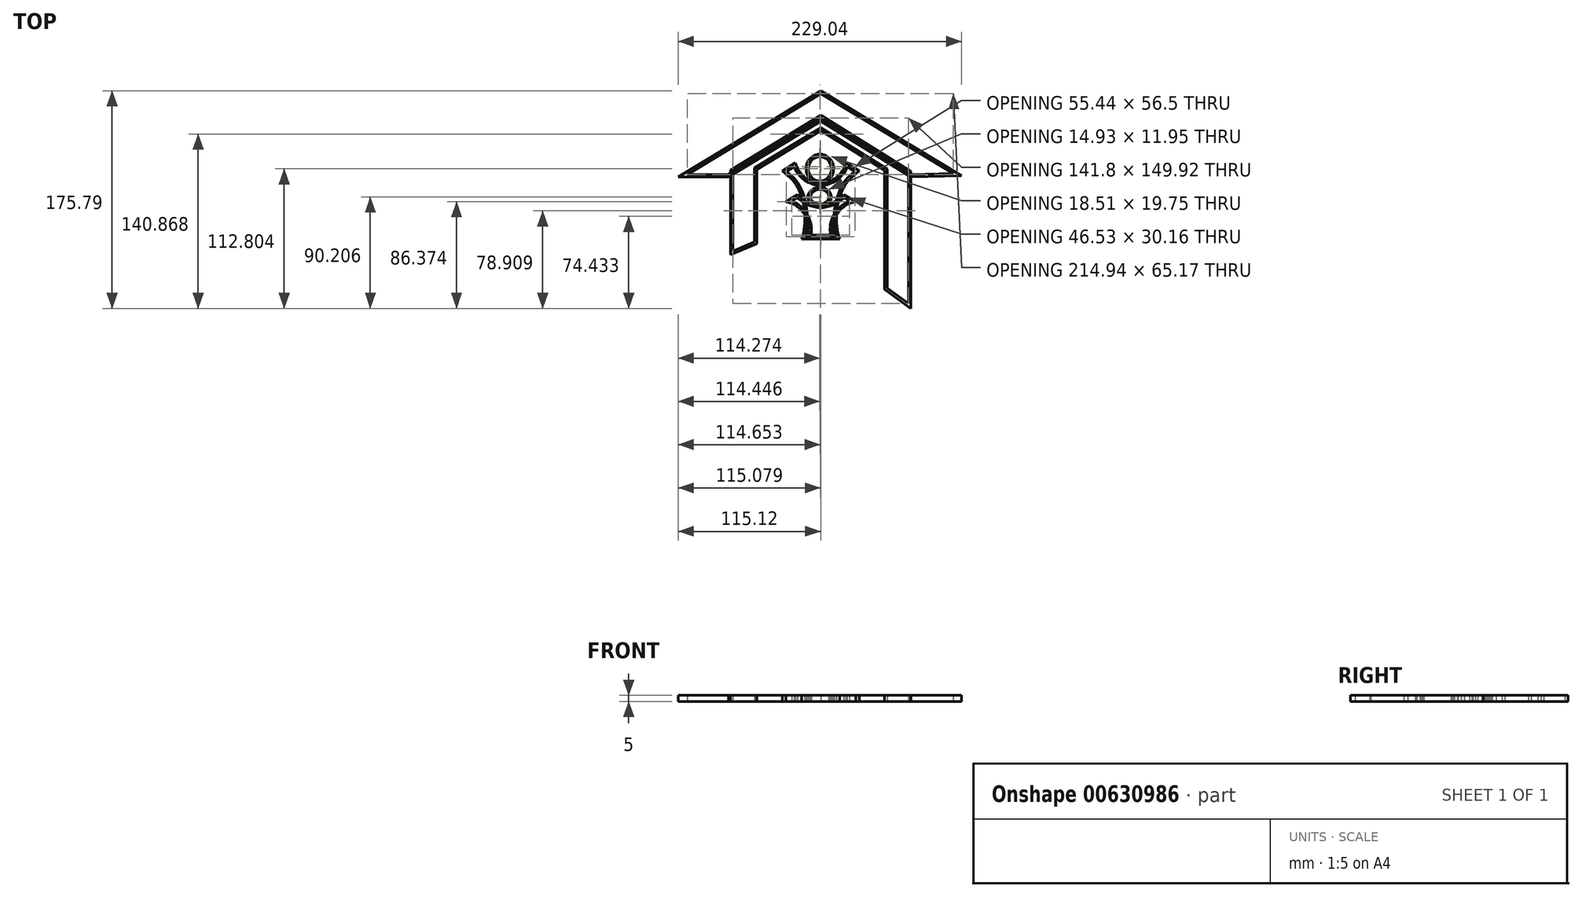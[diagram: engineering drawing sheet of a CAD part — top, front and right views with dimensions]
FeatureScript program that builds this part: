
annotation { "Feature Type Name" : "Feature", "Feature Type Description" : "" }
export const myFeature = defineFeature(function(context is Context, id is Id, definition is map)
    precondition{}
    {
        {
            var Q0;
            Q0=qCreatedBy(makeId("Top.planeOp"),FACE);
            var sketch = newSketch(context, id + "F0", { "sketchPlane" : qUnion([Q0])});
            skLineSegment(sketch, "E0", {"start": v(0, 74.4) * mm, "end": v(107, 10.1) * mm});
            skLineSegment(sketch, "E1", {"start": v(107, 10.1) * mm, "end": v(73.24, 9.22) * mm});
            skLineSegment(sketch, "E2", {"start": v(73.24, 9.22) * mm, "end": v(0, 54.8) * mm});
            skLineSegment(sketch, "E3", {"start": v(0, 54.8) * mm, "end": v(-74.92, 9.22) * mm});
            skLineSegment(sketch, "E4", {"start": v(-74.92, 9.22) * mm, "end": v(-107.94, 9.22) * mm});
            skLineSegment(sketch, "E5", {"start": v(-107.94, 9.22) * mm, "end": v(0, 74.4) * mm});
            skLineSegment(sketch, "E6", {"start": v(-70.94, 11.64) * mm, "end": v(-70.94, -52.76) * mm});
            skLineSegment(sketch, "E7", {"start": v(-70.94, -52.76) * mm, "end": v(-53.55, -45.28) * mm});
            skLineSegment(sketch, "E8", {"start": v(-53.55, -45.28) * mm, "end": v(-53.55, 14.44) * mm});
            skLineSegment(sketch, "E9", {"start": v(-53.55, 14.44) * mm, "end": v(0, 47.03) * mm});
            skLineSegment(sketch, "E10", {"start": v(0, 47.03) * mm, "end": v(53.66, 13.63) * mm});
            skLineSegment(sketch, "E11", {"start": v(53.66, 13.63) * mm, "end": v(53.66, -82.5) * mm});
            skLineSegment(sketch, "E12", {"start": v(53.66, -82.5) * mm, "end": v(70.86, -95.1) * mm});
            skLineSegment(sketch, "E13", {"start": v(70.86, -95.1) * mm, "end": v(70.86, 10.7) * mm});
            skSolve(sketch);
        }
        {
            var Q0;
            Q0=makeQuery(id+"F0.imprint","IMPRINT",FACE,{"disambiguationData":[TD([[makeQuery(id+"F0.imprint","IMPRINT",EDGE,{"derivedFrom":sQuery(id+"F0.wireOp",EDGE,"E0")}),-1.0]])]});
            extrude(context, id + "F1", {"entities" : qUnion([Q0]), "depth" : 5 * mm, "offsetDistance" : 25 * mm});
        }
        {
            var Q0;
            Q0=makeQuery(id+"F1.opExtrude","CAP_FACE",FACE,{"disambiguationData":[OSD([sQuery(id+"F0.wireOp",EDGE,"E0"),sQuery(id+"F0.wireOp",EDGE,"E1"),sQuery(id+"F0.wireOp",EDGE,"E2"),sQuery(id+"F0.wireOp",EDGE,"E3"),sQuery(id+"F0.wireOp",EDGE,"E4"),sQuery(id+"F0.wireOp",EDGE,"E5")])],"isStart":false});
            var Q1;
            Q1=makeQuery(id+"F1.opExtrude","CAP_FACE",FACE,{"disambiguationData":[OSD([sQuery(id+"F0.wireOp",EDGE,"E0"),sQuery(id+"F0.wireOp",EDGE,"E1"),sQuery(id+"F0.wireOp",EDGE,"E2"),sQuery(id+"F0.wireOp",EDGE,"E3"),sQuery(id+"F0.wireOp",EDGE,"E4"),sQuery(id+"F0.wireOp",EDGE,"E5")])],"isStart":true});
            shell(context, id + "F2", {"entities" : qUnion([Q0, Q1]), "thickness" : 2 * mm, "oppositeDirection" : true});
        }
        {
            var Q0;
            {var subQ3=sQuery(id+"F0.wireOp",EDGE,"E6");Q0=makeQuery(id+"F0.imprint","IMPRINT",FACE,{"disambiguationData":[TD([[makeQuery(id+"F0.imprint","IMPRINT",EDGE,{"derivedFrom":subQ3}),1.0]])]});}
            extrude(context, id + "F3", {"entities" : qUnion([Q0]), "depth" : 5 * mm, "offsetDistance" : 25 * mm});
        }
        {
            var Q0;
            Q0=makeQuery(id+"F3.opExtrude","CAP_FACE",FACE,{"disambiguationData":[OSD([sQuery(id+"F0.wireOp",EDGE,"E2"),sQuery(id+"F0.wireOp",EDGE,"E3"),sQuery(id+"F0.wireOp",EDGE,"E6"),sQuery(id+"F0.wireOp",EDGE,"E7"),sQuery(id+"F0.wireOp",EDGE,"E8"),sQuery(id+"F0.wireOp",EDGE,"E9"),sQuery(id+"F0.wireOp",EDGE,"E10"),sQuery(id+"F0.wireOp",EDGE,"E11"),sQuery(id+"F0.wireOp",EDGE,"E12"),sQuery(id+"F0.wireOp",EDGE,"E13")])],"isStart":false});
            var Q1;
            Q1=makeQuery(id+"F3.opExtrude","CAP_FACE",FACE,{"disambiguationData":[OSD([sQuery(id+"F0.wireOp",EDGE,"E2"),sQuery(id+"F0.wireOp",EDGE,"E3"),sQuery(id+"F0.wireOp",EDGE,"E6"),sQuery(id+"F0.wireOp",EDGE,"E7"),sQuery(id+"F0.wireOp",EDGE,"E8"),sQuery(id+"F0.wireOp",EDGE,"E9"),sQuery(id+"F0.wireOp",EDGE,"E10"),sQuery(id+"F0.wireOp",EDGE,"E11"),sQuery(id+"F0.wireOp",EDGE,"E12"),sQuery(id+"F0.wireOp",EDGE,"E13")])],"isStart":true});
            shell(context, id + "F4", {"entities" : qUnion([Q0, Q1]), "thickness" : 2 * mm, "oppositeDirection" : true});
        }
        {
            var Q0;
            Q0=qCreatedBy(makeId("Top.planeOp"),FACE);
            var sketch = newSketch(context, id + "F5", { "sketchPlane" : qUnion([Q0])});
            skArc(sketch, "E14", {"start": v(0, 0) * mm, "mid": v(13.05, 4.61) * mm, "end": v(21.53, 15.56) * mm});
            skLineSegment(sketch, "E15", {"start": v(21.53, 15.56) * mm, "end": v(27.72, 11.73) * mm});
            skFitSpline(sketch, "E16", {"points": [v(27.72, 11.73) * mm, v(19.66, 4.07) * mm, v(14.06, -6.84) * mm, v(11.2, -18.34) * mm, v(10.91, -30.03) * mm, v(11.7, -37) * mm, v(12.68, -40.94) * mm], "startDerivative": vector(-47.12, -39.35) * mm, "endDerivative": vector(9.4, -33.4) * mm});
            skLineSegment(sketch, "E17", {"start": v(12.68, -40.94) * mm, "end": v(0, -40.94) * mm});
            skArc(sketch, "E18.MirrorCS", {"start": v(0, 0) * mm, "mid": v(-13.05, 4.61) * mm, "end": v(-21.53, 15.56) * mm});
            skLineSegment(sketch, "E19.MirrorCS", {"start": v(-21.53, 15.56) * mm, "end": v(-27.72, 11.73) * mm});
            skFitSpline(sketch, "E20.MirrorCS", {"points": [v(-27.72, 11.73) * mm, v(-19.66, 4.07) * mm, v(-14.06, -6.84) * mm, v(-11.2, -18.34) * mm, v(-10.91, -30.03) * mm, v(-11.7, -37) * mm, v(-12.68, -40.94) * mm], "startDerivative": vector(47.12, -39.35) * mm, "endDerivative": vector(-9.4, -33.4) * mm});
            skLineSegment(sketch, "E21.MirrorCS", {"start": v(-12.68, -40.94) * mm, "end": v(0, -40.94) * mm});
            skEllipse(sketch, "E22", {"center": v(-0.67, 13.74) * mm, "majorRadius": 9.87 * mm, "minorRadius": 9.25 * mm, "majorAxis": v(0, 1)});
            skSolve(sketch);
        }
        {
            var Q0;
            Q0 = qSketchRegion(id + "F5", true);
            extrude(context, id + "F6", {"entities" : qUnion([Q0]), "depth" : 5 * mm, "offsetDistance" : 25 * mm});
        }
        {
            var Q0;
            Q0=makeQuery(id+"F6.opExtrude","CAP_FACE",FACE,{"disambiguationData":[OSD([sQuery(id+"F5.wireOp",EDGE,"E14"),sQuery(id+"F5.wireOp",EDGE,"E15"),sQuery(id+"F5.wireOp",EDGE,"E16"),sQuery(id+"F5.wireOp",EDGE,"E17"),sQuery(id+"F5.wireOp",EDGE,"E18.MirrorCS"),sQuery(id+"F5.wireOp",EDGE,"E19.MirrorCS"),sQuery(id+"F5.wireOp",EDGE,"E20.MirrorCS"),sQuery(id+"F5.wireOp",EDGE,"E21.MirrorCS")])],"isStart":false});
            var Q1;
            Q1=makeQuery(id+"F6.opExtrude","CAP_FACE",FACE,{"disambiguationData":[OSD([sQuery(id+"F5.wireOp",EDGE,"E14"),sQuery(id+"F5.wireOp",EDGE,"E15"),sQuery(id+"F5.wireOp",EDGE,"E16"),sQuery(id+"F5.wireOp",EDGE,"E17"),sQuery(id+"F5.wireOp",EDGE,"E18.MirrorCS"),sQuery(id+"F5.wireOp",EDGE,"E19.MirrorCS"),sQuery(id+"F5.wireOp",EDGE,"E20.MirrorCS"),sQuery(id+"F5.wireOp",EDGE,"E21.MirrorCS")])],"isStart":true});
            var Q2;
            Q2=makeQuery(id+"F6.opExtrude","CAP_FACE",FACE,{"disambiguationData":[OSD([sQuery(id+"F5.wireOp",EDGE,"E22")])],"isStart":false});
            var Q3;
            Q3=makeQuery(id+"F6.opExtrude","CAP_FACE",FACE,{"disambiguationData":[OSD([sQuery(id+"F5.wireOp",EDGE,"E22")])],"isStart":true});
            shell(context, id + "F7", {"entities" : qUnion([Q0, Q1, Q2, Q3]), "thickness" : 2 * mm, "oppositeDirection" : true});
        }
        {
            var Q0;
            Q0=qCreatedBy(makeId("Top.planeOp"),FACE);
            var sketch = newSketch(context, id + "F8", { "sketchPlane" : qUnion([Q0])});
            skArc(sketch, "E23", {"start": v(0, -17.68) * mm, "mid": v(10.19, -15.41) * mm, "end": v(18.82, -9.55) * mm});
            skLineSegment(sketch, "E24", {"start": v(18.82, -9.55) * mm, "end": v(23.27, -12.12) * mm});
            skArc(sketch, "E25", {"start": v(23.27, -12.12) * mm, "mid": v(10.71, -23.2) * mm, "end": v(7.9, -39.7) * mm});
            skLineSegment(sketch, "E26", {"start": v(7.9, -39.7) * mm, "end": v(0, -39.7) * mm});
            skArc(sketch, "E27.MirrorCS", {"start": v(0, -17.68) * mm, "mid": v(-10.19, -15.41) * mm, "end": v(-18.82, -9.55) * mm});
            skLineSegment(sketch, "E28.MirrorCS", {"start": v(-18.82, -9.55) * mm, "end": v(-23.27, -12.12) * mm});
            skArc(sketch, "E29.MirrorCS", {"start": v(-23.27, -12.12) * mm, "mid": v(-10.71, -23.2) * mm, "end": v(-7.9, -39.7) * mm});
            skLineSegment(sketch, "E30.MirrorCS", {"start": v(-7.9, -39.7) * mm, "end": v(0, -39.7) * mm});
            skEllipse(sketch, "E31", {"center": v(-0.85, -8.85) * mm, "majorRadius": 5.98 * mm, "minorRadius": 7.47 * mm, "majorAxis": v(0, 1)});
            skSolve(sketch);
        }
        {
            var Q0;
            Q0 = qSketchRegion(id + "F8", true);
            extrude(context, id + "F9", {"entities" : qUnion([Q0]), "depth" : 5 * mm, "offsetDistance" : 25 * mm});
        }
        {
            var Q0;
            Q0=makeQuery(id+"F9.opExtrude","CAP_FACE",FACE,{"disambiguationData":[OSD([sQuery(id+"F8.wireOp",EDGE,"E31")])],"isStart":false});
            var Q1;
            Q1=makeQuery(id+"F9.opExtrude","CAP_FACE",FACE,{"disambiguationData":[OSD([sQuery(id+"F8.wireOp",EDGE,"E23"),sQuery(id+"F8.wireOp",EDGE,"E24"),sQuery(id+"F8.wireOp",EDGE,"E25"),sQuery(id+"F8.wireOp",EDGE,"E26"),sQuery(id+"F8.wireOp",EDGE,"E27.MirrorCS"),sQuery(id+"F8.wireOp",EDGE,"E28.MirrorCS"),sQuery(id+"F8.wireOp",EDGE,"E29.MirrorCS"),sQuery(id+"F8.wireOp",EDGE,"E30.MirrorCS")])],"isStart":false});
            var Q2;
            Q2=makeQuery(id+"F9.opExtrude","CAP_FACE",FACE,{"disambiguationData":[OSD([sQuery(id+"F8.wireOp",EDGE,"E31")])],"isStart":true});
            var Q3;
            Q3=makeQuery(id+"F9.opExtrude","CAP_FACE",FACE,{"disambiguationData":[OSD([sQuery(id+"F8.wireOp",EDGE,"E23"),sQuery(id+"F8.wireOp",EDGE,"E24"),sQuery(id+"F8.wireOp",EDGE,"E25"),sQuery(id+"F8.wireOp",EDGE,"E26"),sQuery(id+"F8.wireOp",EDGE,"E27.MirrorCS"),sQuery(id+"F8.wireOp",EDGE,"E28.MirrorCS"),sQuery(id+"F8.wireOp",EDGE,"E29.MirrorCS"),sQuery(id+"F8.wireOp",EDGE,"E30.MirrorCS")])],"isStart":true});
            shell(context, id + "F10", {"entities" : qUnion([Q0, Q1, Q2, Q3]), "thickness" : 2 * mm, "oppositeDirection" : true});
        }
    });
